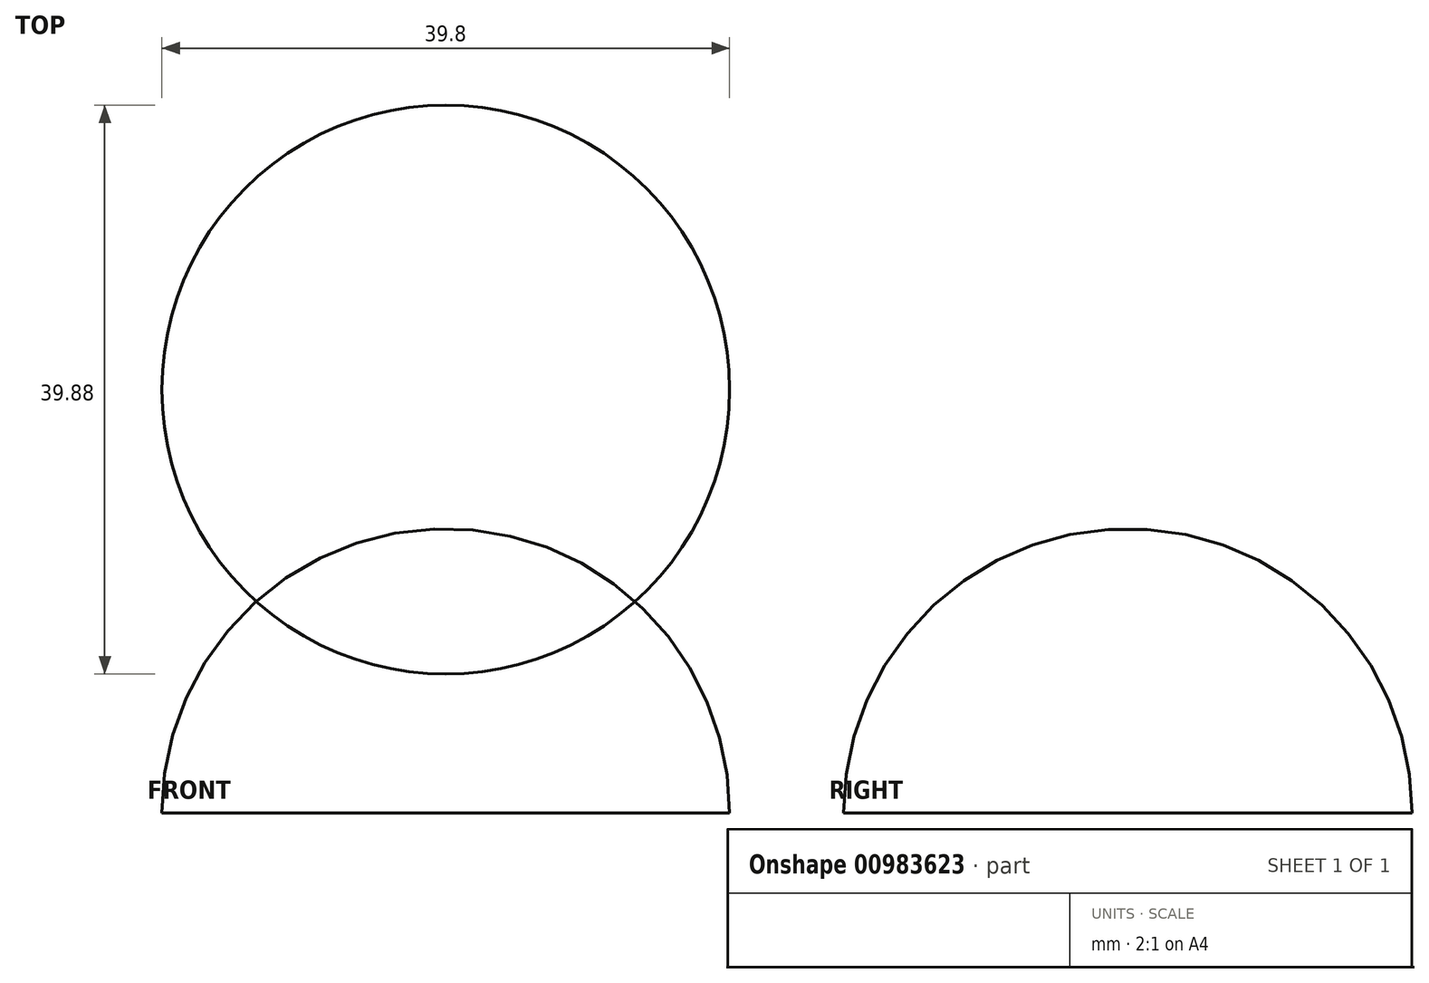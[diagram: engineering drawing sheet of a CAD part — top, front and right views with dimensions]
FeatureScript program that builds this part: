
annotation { "Feature Type Name" : "Feature", "Feature Type Description" : "" }
export const myFeature = defineFeature(function(context is Context, id is Id, definition is map)
    precondition{}
    {
        {
            var Q0;
            Q0=qCreatedBy(makeId("Top.planeOp"),FACE);
            var sketch = newSketch(context, id + "F0", { "sketchPlane" : qUnion([Q0])});
            skLineSegment(sketch, "E0", {"start": v(0, 0) * mm, "end": v(39.8, 0) * mm});
            skArc(sketch, "E1", {"start": v(39.8, 0) * mm, "mid": v(19.9, 19.94) * mm, "end": v(0, 0) * mm});
            skSolve(sketch);
        }
        {
            var Q0;
            Q0=makeQuery(id+"F0.imprint","IMPRINT",FACE,{"disambiguationData":[TD([[makeQuery(id+"F0.imprint","IMPRINT",EDGE,{"derivedFrom":sQuery(id+"F0.wireOp",EDGE,"E0")}),1.0]])]});
            var Q1;
            Q1=sQuery(id+"F0.wireOp",EDGE,"E0");
            revolve(context, id + "F1", {"surfaceOperationType" : NewSurfaceOperationType.NEW, "entities" : qUnion([Q0]), "axis" : qUnion([Q1]), "revolveType" : RevolveType.ONE_DIRECTION, "angle" : 180 * degree});
        }
    });
